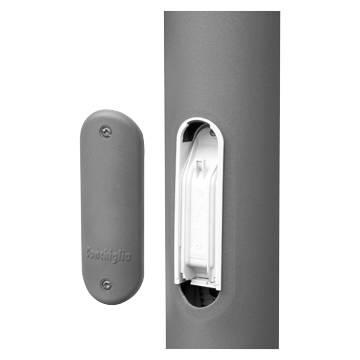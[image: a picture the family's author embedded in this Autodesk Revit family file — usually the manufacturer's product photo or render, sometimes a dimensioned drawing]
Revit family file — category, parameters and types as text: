
# Revit family: Lighting-ArredoUrbano-GEWISS-URBAN[O3]-PALI_CONICI
name_source: partatom
category: Apparecchi per illuminazione
units: mm (PartAtom-declared; Revit-internal decimal feet)

## family parameters
Condiviso = No
Host = Superficie
Numero OmniClass = 23.80.00.00
Punto di calcolo locali = Sì
Quota connettore circolare = Usa diametro
Sorgente d'illuminazione = No
Taglio con vuoti quando caricato = No
Tipo di parte = Normale
Titolo OmniClass = Electric Power and Lighting

## types (1)
- Lighting-ArredoUrbano-GEWISS-URBAN[O3]-PALI_CONICI
    Altezza palo = 8800 mm  [stored 28.8714 ft]
    Catalogo = LIGHTING
    Catalogo Serie = STREET [O3]
    Codice EAN = 8011564782587
    Codice Electrocod = 240
    Colore = Grigio grafite
    Descrizione = STREET PALO CONICO 8,8m GRIGIO GRAFITE
    Diametro = 60 mm  [stored 0.19685 ft]
    Diametro base (mm) = 148
    Diametro inferiore = 148 mm  [stored 0.485564 ft]
    Diametro sommità (mm) = 60
    Finitura = Verniciato
    IDF = 0b45d6f1-ece2-47e2-922c-18e9a9c1b305
    IDT = fb51b8d7-080d-47f3-85ad-856ae9a19558
    Immagine tipo = GW84096.jpg
    Interramento (m) = 0,8
    Lunghezza totale (m) = 8,8
    Materiale = Acciaio zincato
    Modello = GW87592
    Palo = <Per categoria>
    Peso (kg) = 91
    Peso (kg): = 91
    Produttore = GEWISS S.p.A.
    Prospetto di default = 1219 mm
    SEO = Palo
    Scheda Tecnica = https://www.gewiss.com
    Tipo: = Conico
    URL = https://www.gewiss.com
    Versione file RFA = 20.11

note: [stored X ft] marks values corroborated as IEEE doubles in the binary element streams (Revit-internal decimal feet)

## geometry (parser evidence)
native form markers: Blend x2
no freeform markers — native parametric forms only
